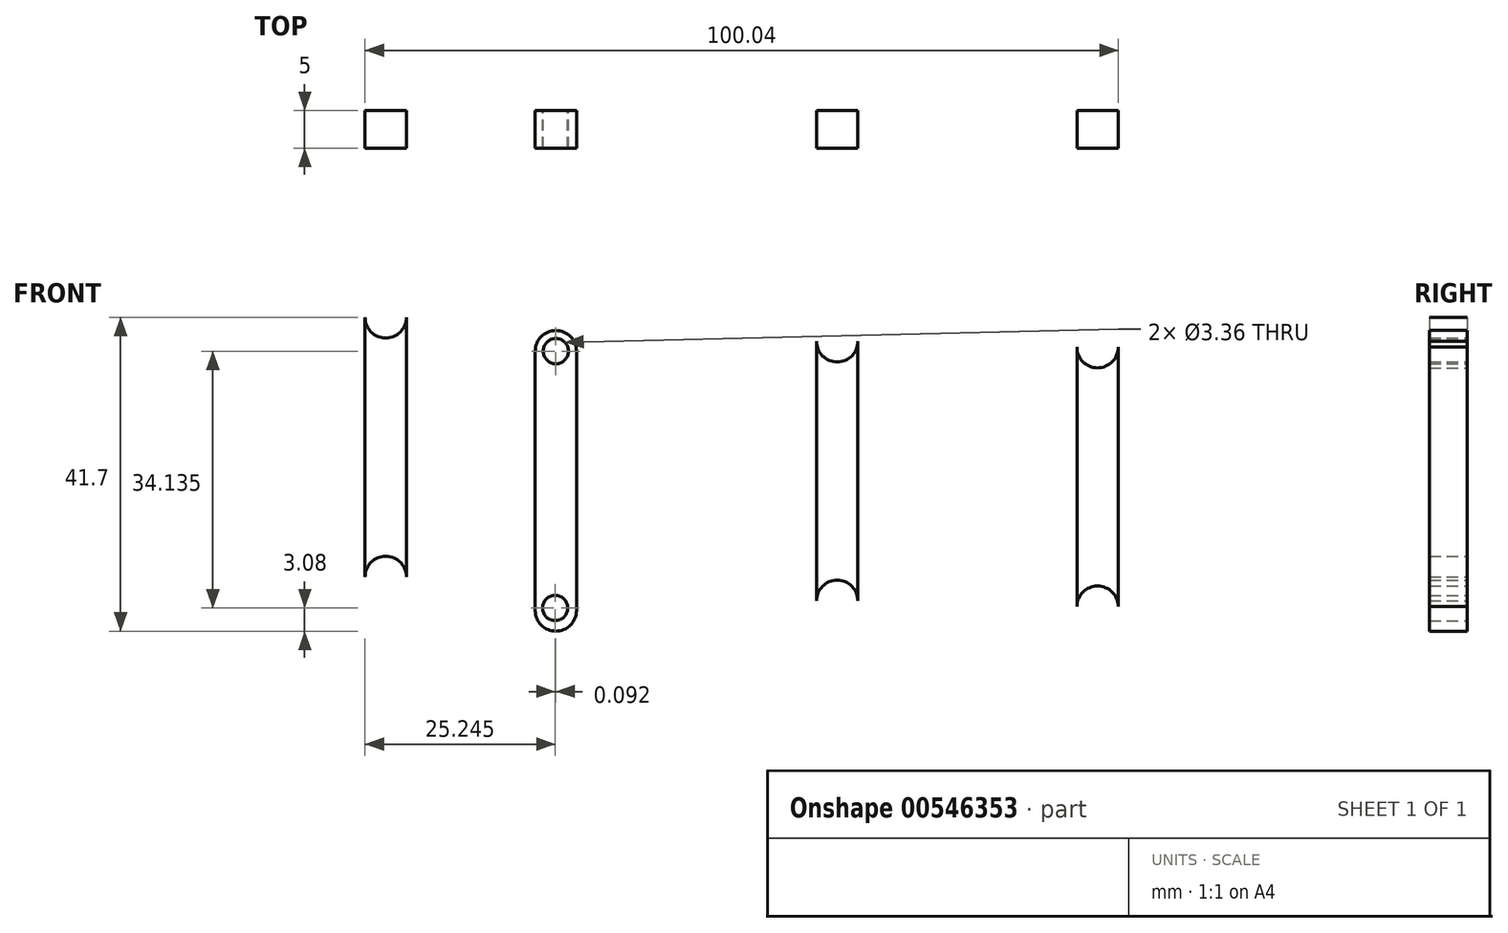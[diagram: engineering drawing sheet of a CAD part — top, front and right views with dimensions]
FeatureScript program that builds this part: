
annotation { "Feature Type Name" : "Feature", "Feature Type Description" : "" }
export const myFeature = defineFeature(function(context is Context, id is Id, definition is map)
    precondition{}
    {
        {
            var Q0;
            Q0=qCreatedBy(makeId("Front.planeOp"),FACE);
            var sketch = newSketch(context, id + "F0", { "sketchPlane" : qUnion([Q0])});
            skLineSegment(sketch, "E0.bottom", {"start": v(-29.51, 6.14) * mm, "end": v(-24.03, 6.14) * mm});
            skLineSegment(sketch, "E0.top", {"start": v(-29.51, -28.34) * mm, "end": v(-24.03, -28.34) * mm});
            skLineSegment(sketch, "E0.left", {"start": v(-29.51, 6.14) * mm, "end": v(-29.51, -28.34) * mm});
            skLineSegment(sketch, "E0.right", {"start": v(-24.03, 6.14) * mm, "end": v(-24.03, -28.34) * mm});
            skCircle(sketch, "E1", {"center": v(-26.77, 6.14) * mm, "radius": 2.74 * mm});
            skCircle(sketch, "E2", {"center": v(-26.77, -28.34) * mm, "radius": 2.74 * mm});
            skCircle(sketch, "E3.MirrorC", {"center": v(10.6, -27.04) * mm, "radius": 2.74 * mm});
            skCircle(sketch, "E4.MirrorC", {"center": v(10.6, 7.44) * mm, "radius": 2.74 * mm});
            skLineSegment(sketch, "E5.MirrorCS", {"start": v(13.34, 7.44) * mm, "end": v(13.34, -27.04) * mm});
            skLineSegment(sketch, "E6", {"start": v(7.86, 7.44) * mm, "end": v(7.86, -27.04) * mm});
            skPoint(sketch, "E7.MirrorCS.end.orphan", {"position": v(-24.03, 6.14) * mm});
            skPoint(sketch, "E7.MirrorCS.start.orphan", {"position": v(-18.54, 6.14) * mm});
            skPoint(sketch, "E8.MirrorCS.end.orphan", {"position": v(-24.03, -28.34) * mm});
            skPoint(sketch, "E8.MirrorCS.start.orphan", {"position": v(-18.54, -28.34) * mm});
            skCircle(sketch, "E9.MirrorC", {"center": v(45.19, -27.82) * mm, "radius": 2.74 * mm});
            skCircle(sketch, "E10.MirrorC", {"center": v(45.19, 6.66) * mm, "radius": 2.74 * mm});
            skLineSegment(sketch, "E11.MirrorCS", {"start": v(47.93, 6.66) * mm, "end": v(47.93, -27.82) * mm});
            skLineSegment(sketch, "E12", {"start": v(42.44, 6.66) * mm, "end": v(42.44, -27.82) * mm});
            skCircle(sketch, "E13.MirrorC", {"center": v(-49.37, -23.86) * mm, "radius": 2.74 * mm});
            skCircle(sketch, "E14.MirrorC", {"center": v(-49.37, 10.62) * mm, "radius": 2.74 * mm});
            skLineSegment(sketch, "E15.MirrorCS", {"start": v(-46.62, 10.62) * mm, "end": v(-46.62, -23.86) * mm});
            skLineSegment(sketch, "E16", {"start": v(-52.1, 10.62) * mm, "end": v(-52.1, -23.86) * mm});
            skSolve(sketch);
        }
        {
            var Q0;
            Q0=qCreatedBy(makeId("Front.planeOp"),FACE);
            var sketch = newSketch(context, id + "F1", { "sketchPlane" : qUnion([Q0])});
            skCircle(sketch, "E17", {"center": v(-49.43, 10.71) * mm, "radius": 1.89 * mm});
            skCircle(sketch, "E18", {"center": v(-49.24, -23.9) * mm, "radius": 1.89 * mm});
            skCircle(sketch, "E19", {"center": v(-26.7, 6.38) * mm, "radius": 1.89 * mm});
            skCircle(sketch, "E20", {"center": v(-26.86, -28) * mm, "radius": 1.89 * mm});
            skCircle(sketch, "E21", {"center": v(10.57, -27.2) * mm, "radius": 1.89 * mm});
            skCircle(sketch, "E22", {"center": v(10.57, 7.68) * mm, "radius": 1.89 * mm});
            skCircle(sketch, "E23", {"center": v(45.28, 6.61) * mm, "radius": 1.89 * mm});
            skCircle(sketch, "E24", {"center": v(45.12, -27.6) * mm, "radius": 1.89 * mm});
            skSolve(sketch);
        }
        {
            var Q0;
            {var subQ0=sQuery(id+"F0.wireOp",EDGE,"E0.bottom");Q0=makeQuery(id+"F0.imprint","IMPRINT",FACE,{"disambiguationData":[TD([[makeQuery(id+"F0.imprint","IMPRINT",EDGE,{"derivedFrom":subQ0}),1.0]])]});}
            var Q1;
            {var subQ0=sQuery(id+"F0.wireOp",EDGE,"E0.bottom");Q1=makeQuery(id+"F0.imprint","IMPRINT",FACE,{"disambiguationData":[TD([[makeQuery(id+"F0.imprint","IMPRINT",EDGE,{"derivedFrom":subQ0}),-1.0]])]});}
            var Q2;
            {var subQ0=sQuery(id+"F0.wireOp",EDGE,"E0.left");Q2=makeQuery(id+"F0.imprint","IMPRINT",FACE,{"disambiguationData":[TD([[makeQuery(id+"F0.imprint","IMPRINT",EDGE,{"derivedFrom":subQ0}),1.0]])]});}
            var Q3;
            {var subQ0=sQuery(id+"F0.wireOp",EDGE,"E0.top");Q3=makeQuery(id+"F0.imprint","IMPRINT",FACE,{"disambiguationData":[TD([[makeQuery(id+"F0.imprint","IMPRINT",EDGE,{"derivedFrom":subQ0}),1.0]])]});}
            var Q4;
            {var subQ0=sQuery(id+"F0.wireOp",EDGE,"E0.top");Q4=makeQuery(id+"F0.imprint","IMPRINT",FACE,{"disambiguationData":[TD([[makeQuery(id+"F0.imprint","IMPRINT",EDGE,{"derivedFrom":subQ0}),-1.0]])]});}
            extrude(context, id + "F2", {"entities" : qUnion([Q0, Q1, Q2, Q3, Q4]), "depth" : 5 * mm, "offsetDistance" : 25 * mm});
        }
        {
            var Q0;
            {var subQ0=sQuery(id+"F0.wireOp",EDGE,"E3.MirrorC");var subQ1=makeQuery(id+"F0.imprint","INTERSECT",VERTEX,{"derivedFrom":[subQ0,sQuery(id+"F0.wireOp",EDGE,"E5.MirrorCS")]});Q0=makeQuery(id+"F0.imprint","IMPRINT",FACE,{"disambiguationData":[TD([[makeQuery(id+"F0.imprint","IMPRINT",EDGE,{"disambiguationData":[TD([[subQ1,1.0]])],"derivedFrom":subQ0}),-1.0]])]});}
            var Q1;
            {var subQ0=sQuery(id+"F0.wireOp",EDGE,"E4.MirrorC");var subQ1=makeQuery(id+"F0.imprint","INTERSECT",VERTEX,{"derivedFrom":[subQ0,sQuery(id+"F0.wireOp",EDGE,"E5.MirrorCS")]});Q1=makeQuery(id+"F0.imprint","IMPRINT",FACE,{"disambiguationData":[TD([[makeQuery(id+"F0.imprint","IMPRINT",EDGE,{"disambiguationData":[TD([[subQ1,1.0]])],"derivedFrom":subQ0}),-1.0]])]});}
            var Q2;
            {var subQ0=sQuery(id+"F0.wireOp",EDGE,"E5.MirrorCS");Q2=makeQuery(id+"F0.imprint","IMPRINT",FACE,{"disambiguationData":[TD([[makeQuery(id+"F0.imprint","IMPRINT",EDGE,{"derivedFrom":subQ0}),-1.0]])]});}
            extrude(context, id + "F3", {"entities" : qUnion([Q0, Q1, Q2]), "depth" : 5 * mm, "offsetDistance" : 25 * mm});
        }
        {
            var Q0;
            {var subQ0=sQuery(id+"F0.wireOp",EDGE,"E15.MirrorCS");Q0=makeQuery(id+"F0.imprint","IMPRINT",FACE,{"disambiguationData":[TD([[makeQuery(id+"F0.imprint","IMPRINT",EDGE,{"derivedFrom":subQ0}),-1.0]])]});}
            var Q1;
            {var subQ0=sQuery(id+"F0.wireOp",EDGE,"E13.MirrorC");var subQ1=makeQuery(id+"F0.imprint","INTERSECT",VERTEX,{"derivedFrom":[subQ0,sQuery(id+"F0.wireOp",EDGE,"E15.MirrorCS")]});Q1=makeQuery(id+"F0.imprint","IMPRINT",FACE,{"disambiguationData":[TD([[makeQuery(id+"F0.imprint","IMPRINT",EDGE,{"disambiguationData":[TD([[subQ1,1.0]])],"derivedFrom":subQ0}),-1.0]])]});}
            var Q2;
            {var subQ0=sQuery(id+"F0.wireOp",EDGE,"E14.MirrorC");var subQ1=makeQuery(id+"F0.imprint","INTERSECT",VERTEX,{"derivedFrom":[subQ0,sQuery(id+"F0.wireOp",EDGE,"E15.MirrorCS")]});Q2=makeQuery(id+"F0.imprint","IMPRINT",FACE,{"disambiguationData":[TD([[makeQuery(id+"F0.imprint","IMPRINT",EDGE,{"disambiguationData":[TD([[subQ1,1.0]])],"derivedFrom":subQ0}),-1.0]])]});}
            var Q3;
            {var subQ0=sQuery(id+"F0.wireOp",EDGE,"E9.MirrorC");var subQ1=makeQuery(id+"F0.imprint","INTERSECT",VERTEX,{"derivedFrom":[subQ0,sQuery(id+"F0.wireOp",EDGE,"E11.MirrorCS")]});Q3=makeQuery(id+"F0.imprint","IMPRINT",FACE,{"disambiguationData":[TD([[makeQuery(id+"F0.imprint","IMPRINT",EDGE,{"disambiguationData":[TD([[subQ1,1.0]])],"derivedFrom":subQ0}),-1.0]])]});}
            var Q4;
            {var subQ0=sQuery(id+"F0.wireOp",EDGE,"E10.MirrorC");var subQ1=makeQuery(id+"F0.imprint","INTERSECT",VERTEX,{"derivedFrom":[subQ0,sQuery(id+"F0.wireOp",EDGE,"E11.MirrorCS")]});Q4=makeQuery(id+"F0.imprint","IMPRINT",FACE,{"disambiguationData":[TD([[makeQuery(id+"F0.imprint","IMPRINT",EDGE,{"disambiguationData":[TD([[subQ1,1.0]])],"derivedFrom":subQ0}),-1.0]])]});}
            var Q5;
            {var subQ0=sQuery(id+"F0.wireOp",EDGE,"E11.MirrorCS");Q5=makeQuery(id+"F0.imprint","IMPRINT",FACE,{"disambiguationData":[TD([[makeQuery(id+"F0.imprint","IMPRINT",EDGE,{"derivedFrom":subQ0}),-1.0]])]});}
            extrude(context, id + "F4", {"entities" : qUnion([Q0, Q1, Q2, Q3, Q4, Q5]), "depth" : 5 * mm, "offsetDistance" : 25 * mm});
        }
        {
            var Q0;
            Q0=sQuery(id+"F0.wireOp",VERTEX,"E10.MirrorC.center");
            var Q1;
            Q1=sQuery(id+"F0.wireOp",VERTEX,"E9.MirrorC.center");
            var Q2;
            Q2=sQuery(id+"F0.wireOp",VERTEX,"E3.MirrorC.center");
            var Q3;
            Q3=sQuery(id+"F0.wireOp",VERTEX,"E4.MirrorC.center");
            var Q4;
            Q4=sQuery(id+"F0.wireOp",VERTEX,"E1.center");
            var Q5;
            Q5=sQuery(id+"F1.wireOp",VERTEX,"E20.center");
            var Q6;
            Q6=sQuery(id+"F1.wireOp",VERTEX,"E18.center");
            var Q7;
            Q7=sQuery(id+"F0.wireOp",VERTEX,"E14.MirrorC.center");
            var Q8;
            Q8=makeQuery(id+"F4.opExtrude","SWEPT_BODY",BODY,{"disambiguationData":[OSD([sQuery(id+"F0.wireOp",EDGE,"E9.MirrorC"),sQuery(id+"F0.wireOp",EDGE,"E10.MirrorC"),sQuery(id+"F0.wireOp",EDGE,"E11.MirrorCS"),sQuery(id+"F0.wireOp",EDGE,"E12")])]});
            var Q9;
            Q9=makeQuery(id+"F3.opExtrude","SWEPT_BODY",BODY,{"disambiguationData":[OSD([sQuery(id+"F0.wireOp",EDGE,"E3.MirrorC"),sQuery(id+"F0.wireOp",EDGE,"E4.MirrorC"),sQuery(id+"F0.wireOp",EDGE,"E5.MirrorCS"),sQuery(id+"F0.wireOp",EDGE,"E6")])]});
            var Q10;
            Q10=makeQuery(id+"F2.opExtrude","SWEPT_BODY",BODY,{"disambiguationData":[OSD([sQuery(id+"F0.wireOp",EDGE,"E0.left"),sQuery(id+"F0.wireOp",EDGE,"E0.right"),sQuery(id+"F0.wireOp",EDGE,"E1"),sQuery(id+"F0.wireOp",EDGE,"E2")])]});
            var Q11;
            Q11=makeQuery(id+"F4.opExtrude","SWEPT_BODY",BODY,{"disambiguationData":[OSD([sQuery(id+"F0.wireOp",EDGE,"E13.MirrorC"),sQuery(id+"F0.wireOp",EDGE,"E14.MirrorC"),sQuery(id+"F0.wireOp",EDGE,"E15.MirrorCS"),sQuery(id+"F0.wireOp",EDGE,"E16")])]});
            hole(context, id + "F5", {"style" : HoleStyle.SIMPLE, "endStyle" : HoleEndStyle.THROUGH, "oppositeDirection" : true, "holeDiameter" : 3.36 * mm, "isTappedThrough" : true, "tappedDepth" : 12 * mm, "tapClearance" : 3, "locations" : qUnion([Q0, Q1, Q2, Q3, Q4, Q5, Q6, Q7]), "scope" : qUnion([Q8, Q9, Q10, Q11])});
        }
    });
